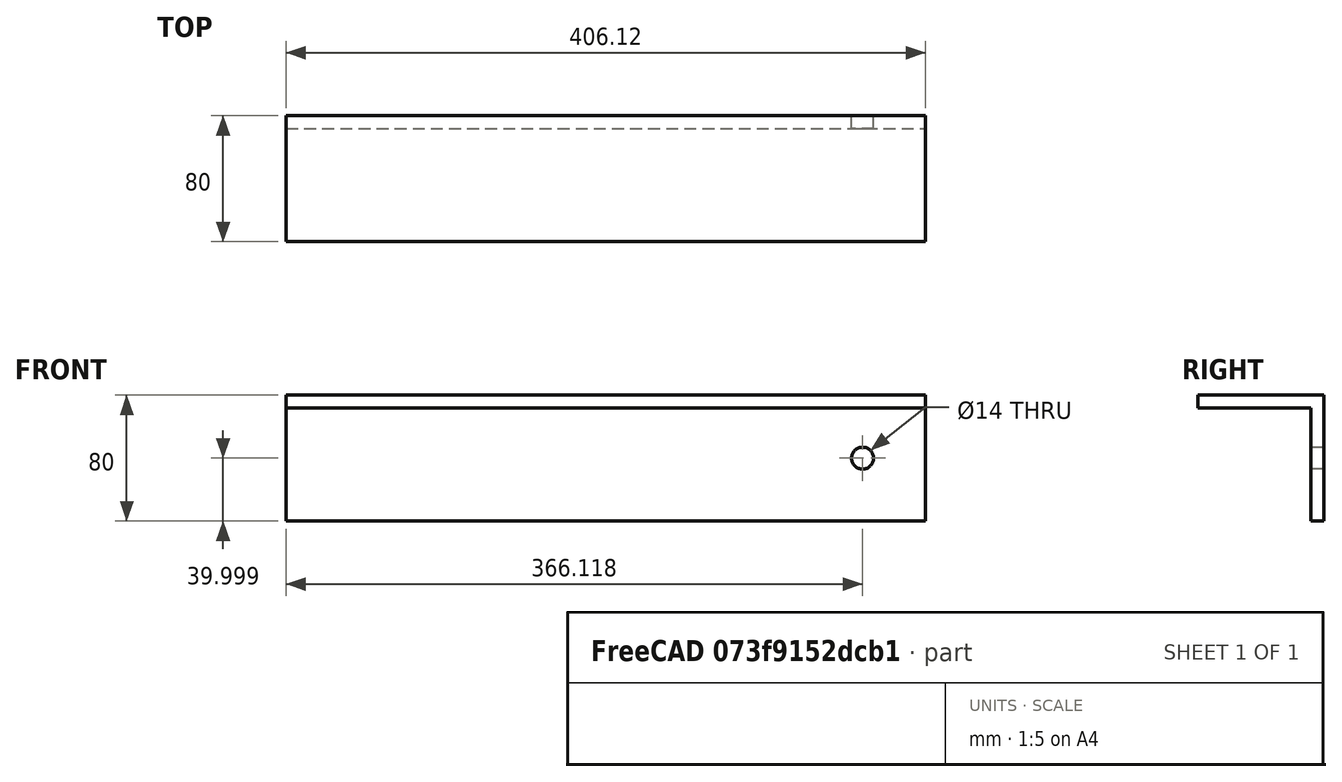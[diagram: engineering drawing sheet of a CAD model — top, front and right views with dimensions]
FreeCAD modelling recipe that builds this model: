
FCSTD DOCUMENT  (FreeCAD 1.0R39109 (Git))
Label: Frame_Shape_Star
License: All rights reserved
LicenseURL: http://en.wikipedia.org/wiki/All_rights_reserved
objects: App::Link×2, Spreadsheet::Sheet×1, Part::Mirroring×1, App::Part×1
note: 1 computed .brp shape members not serialized (recipe doc carries the construction recipe); baked Part::Feature solids carry a one-line shape summary decoded from their .brp
EXTERNAL_REF file=Frame_Shape_H.FCStd obj=Part
EXTERNAL_REF file=Frame_Bracket_Middle.FCStd obj=Body
EXTERNAL_REF file=../../Master_of_Puppets.FCStd obj=Alternator
EXTERNAL_REF file=../../Master_of_Puppets.FCStd obj=Spreadsheet

FEATURE [App::Link] Link  label="Shape_H"
  LinkedObject = -> <external Frame_Shape_H.FCStd>#Part
FEATURE [App::Link] Link001  label="Bracket_Middle_Left"
  LinkPlacement = pos=(0,0,386.349) rot=(0,0,1;0rad)
  LinkTransform = true
  LinkedObject = -> <external Frame_Bracket_Middle.FCStd>#Body
  Placement = pos=(0,0,386.349) rot=(0,0,1;0rad)
  expr: .LinkPlacement.Base.z = Spreadsheet.MiddleBracketZ
FEATURE [Spreadsheet::Sheet] Spreadsheet
  cells = A1='Inputs; A2='MetalLengthL; B2(MetalLengthL)==Master_of_Puppets#Spreadsheet.MetalLengthL; A3='ChannelSectionHeight; B3(ChannelSectionHeight)==Master_of_Puppets#Alternator.B; A4='Calculated; A5='MiddleBracketZ; B5(MiddleBracketZ)==(MetalLengthL + ChannelSectionHeight) / 2
FEATURE [Part::Mirroring] mirror  label="Bracket_Middle_Right"
  Base = (1.52588e-05,25,141.71)
  Normal = (1,0,-1.19209e-07)
  Source = -> Link001
FEATURE [App::Part] Part  label="Frame_Shape_Star"
  Group = -> [Link,Link001,mirror]
  Origin = -> Origin

RESOLVED EXTERNAL PARTS (link-assembly join: the EXTERNAL_REF files above that resolve inside this repo's crawl, each included once):
---- part ../../Master_of_Puppets.FCStd = doc fcstd_6404554055c4 (61625 chars; too large to inline — full recipe in that document) ----
---- part Frame_Bracket_Middle.FCStd = doc fcstd_d9f791926894 ----
FCSTD DOCUMENT  (FreeCAD 0.20R29177 (Git))
Label: Frame_Bracket_Middle
License: All rights reserved
LicenseURL: http://en.wikipedia.org/wiki/All_rights_reserved
objects: Sketcher::SketchObject×2, Spreadsheet::Sheet×1, PartDesign::Pad×1, PartDesign::Pocket×1, PartDesign::Body×1
note: 7 computed .brp shape members not serialized (recipe doc carries the construction recipe); baked Part::Feature solids carry a one-line shape summary decoded from their .brp
EXTERNAL_REF file=../../Master_of_Puppets.FCStd obj=Alternator
EXTERNAL_REF file=../../Master_of_Puppets.FCStd obj=Spreadsheet

FEATURE [Spreadsheet::Sheet] Spreadsheet
  cells = A1=Inputs; A2=MetalThicknessL; B2(MetalThicknessL)==Master_of_Puppets#Spreadsheet.MetalThicknessL; A3=MetalLengthL; B3(MetalLengthL)==Master_of_Puppets#Spreadsheet.MetalLengthL; A4=HolesRadius; B4(HolesRadius)==Master_of_Puppets#Alternator.HolesRadius; A5=StatorHolesCircumradius; B5(StatorHolesCircumradius)==Master_of_Puppets#Alternator.StatorHolesCircumradius; A6=CC; B6(CC)==Master_of_Puppets#Alternator.CC; A7=Placement; A8=X; B8(X)==-MetalLengthL; A9=Y; B9(Y)==MetalLengthL
FEATURE [Sketcher::SketchObject] Sketch
  FullyConstrained = true
  MapMode = 5
  Placement = pos=(0,0,0) rot=(0.57735,0.57735,0.57735;2.0944rad)
  Support = -> [YZ_Plane]
  expr: Constraints[15] = Spreadsheet.MetalLengthL
  expr: Constraints[16] = Spreadsheet.MetalThicknessL
  sketch-geometry (6):
    g0: LineSegment StartX=0 StartY=0 StartZ=0 EndX=0 EndY=80 EndZ=0
    g1: LineSegment StartX=0 StartY=80 StartZ=0 EndX=8 EndY=80 EndZ=0
    g2: LineSegment StartX=8 StartY=80 StartZ=0 EndX=8 EndY=8 EndZ=0
    g3: LineSegment StartX=8 StartY=8 StartZ=0 EndX=80 EndY=8 EndZ=0
    g4: LineSegment StartX=80 StartY=8 StartZ=0 EndX=80 EndY=0 EndZ=0
    g5: LineSegment StartX=80 StartY=0 StartZ=0 EndX=0 EndY=0 EndZ=0
  constraints (17):
    c: Coincident(g-1,g0)
    c: PointOnObject(g0,g-2)
    c: Coincident(g0,g1)
    c: Horizontal(g1)
    c: Coincident(g1,g2)
    c: Vertical(g2)
    c: Coincident(g2,g3)
    c: Horizontal(g3)
    c: Coincident(g3,g4)
    c: Vertical(g4)
    c: Coincident(g4,g5)
    c: Coincident(g5,g0)
    c: Horizontal(g5)
    c: Equal(g1,g4)
    c: Equal(g5,g0)
    c: DistanceX(g5,g5) = 80
    c: DistanceX(g1,g1) = 8
FEATURE [PartDesign::Pad] Pad
  AllowMultiFace = false
  Direction = (1,-1.129e-13,1.129e-13)
  Length = 372.752
  Length2 = 100
  Placement = pos=(0,0,0) rot=(0.57735,0.57735,0.57735;2.0944rad)
  Profile = -> Sketch
  Type = 0
  expr: Length = Spreadsheet.CC
FEATURE [Sketcher::SketchObject] Sketch001
  ExternalGeometry = -> [Pad]
  FullyConstrained = true
  MapMode = 5
  Placement = pos=(0,0,0) rot=(0.707107,0.707107,0;3.14159rad)
  Support = -> [Pad]
  expr: Constraints[1] = Spreadsheet.HolesRadius
  expr: Constraints[2] = Spreadsheet.StatorHolesCircumradius
  expr: Constraints[3] = Spreadsheet.MetalLengthL
  expr: Constraints[4] = 0.5 * Spreadsheet.MetalLengthL
  expr: Constraints[5] = 0.5 * Spreadsheet.MetalLengthL
  sketch-geometry (2):
    g0: Circle CenterX=40 CenterY=-80 CenterZ=0 NormalX=0 NormalY=0 NormalZ=1 AngleXU=0 Radius=412.752
    g1: Circle CenterX=40 CenterY=332.752 CenterZ=0 NormalX=0 NormalY=0 NormalZ=1 AngleXU=0 Radius=7
  constraints (6):
    c: PointOnObject(g1,g0)
    c: Radius(g1) = 7
    c: Radius(g0) = 412.752
    c: Distance(g0,g-3) = 80
    c: Distance(g0,g-2) = 40
    c: DistanceX(g-2,g1) = 40
FEATURE [PartDesign::Pocket] Pocket
  AllowMultiFace = false
  BaseFeature = -> Pad
  Direction = (-1.13e-13,1.129e-13,1)
  Length = 5
  Length2 = 100
  Placement = pos=(0,0,0) rot=(0.57735,0.57735,0.57735;2.0944rad)
  Profile = -> Sketch001
  Type = 1
FEATURE [PartDesign::Body] Body  label="Frame_Bracket_Middle"
  Group = -> [Sketch,Pad,Sketch001,Pocket]
  Origin = -> Origin
  Placement = pos=(-80,80,0) rot=(0,0.707107,-0.707107;3.14159rad)
  Tip = -> Pocket
  expr: .Placement.Base.x = Spreadsheet.X
  expr: .Placement.Base.y = Spreadsheet.Y
---- part Frame_Shape_H.FCStd = doc fcstd_aed3d7aa8fba ----
FCSTD DOCUMENT  (FreeCAD 1.0R39109 (Git))
Label: Frame_Shape_H
License: All rights reserved
LicenseURL: http://en.wikipedia.org/wiki/All_rights_reserved
objects: App::Link×3, Spreadsheet::Sheet×1, App::Part×1
EXTERNAL_REF file=Frame_Channel.FCStd obj=Body
EXTERNAL_REF file=Frame_Bracket_End_TwoHole.FCStd obj=PadBody
EXTERNAL_REF file=../../Master_of_Puppets.FCStd obj=Alternator
EXTERNAL_REF file=../../Master_of_Puppets.FCStd obj=Spreadsheet

FEATURE [App::Link] Link  label="Channel"
  LinkTransform = true
  LinkedObject = -> <external Frame_Channel.FCStd>#Body
FEATURE [App::Link] Link001  label="Bracket_End_TwoHole_Bottom"
  LinkTransform = true
  LinkedObject = -> <external Frame_Bracket_End_TwoHole.FCStd>#PadBody
FEATURE [App::Link] Link002  label="Bracket_End_TwoHole_Top"
  LinkPlacement = pos=(0,0,238.75) rot=(0,1,0;-3.14159rad)
  LinkTransform = true
  LinkedObject = -> <external Frame_Bracket_End_TwoHole.FCStd>#PadBody
  Placement = pos=(0,0,238.75) rot=(0,1,0;-3.14159rad)
  expr: .LinkPlacement.Base.z = Spreadsheet.ChannelSectionHeight
FEATURE [Spreadsheet::Sheet] Spreadsheet
  cells = A1='Inputs; A2='CalculatedWindTurbineShape; B2(CalculatedWindTurbineShape)==Master_of_Puppets#Spreadsheet.CalculatedWindTurbineShape; A3='Channel Section Height; A4='TShapeChannelSectionHeight; B4(TShapeChannelSectionHeight)==Master_of_Puppets#Alternator.BC; A5='HShapeChannelSectionHeight; B5(HShapeChannelSectionHeight)==Master_of_Puppets#Alternator.HH; A6='StarShapeChannelSectionHeight; B6(StarShapeChannelSectionHeight)==Master_of_Puppets#Alternator.B; A7='ChannelSectionHeight; B7(ChannelSectionHeight)==CalculatedWindTurbineShape == <<T>> ? TShapeChannelSectionHeight : (CalculatedWindTurbineShape == <<H>> ? HShapeChannelSectionHeight : StarShapeChannelSectionHeight)
FEATURE [App::Part] Part  label="Frame_Shape_H"
  Group = -> [Link,Link001,Link002]
  Origin = -> Origin
